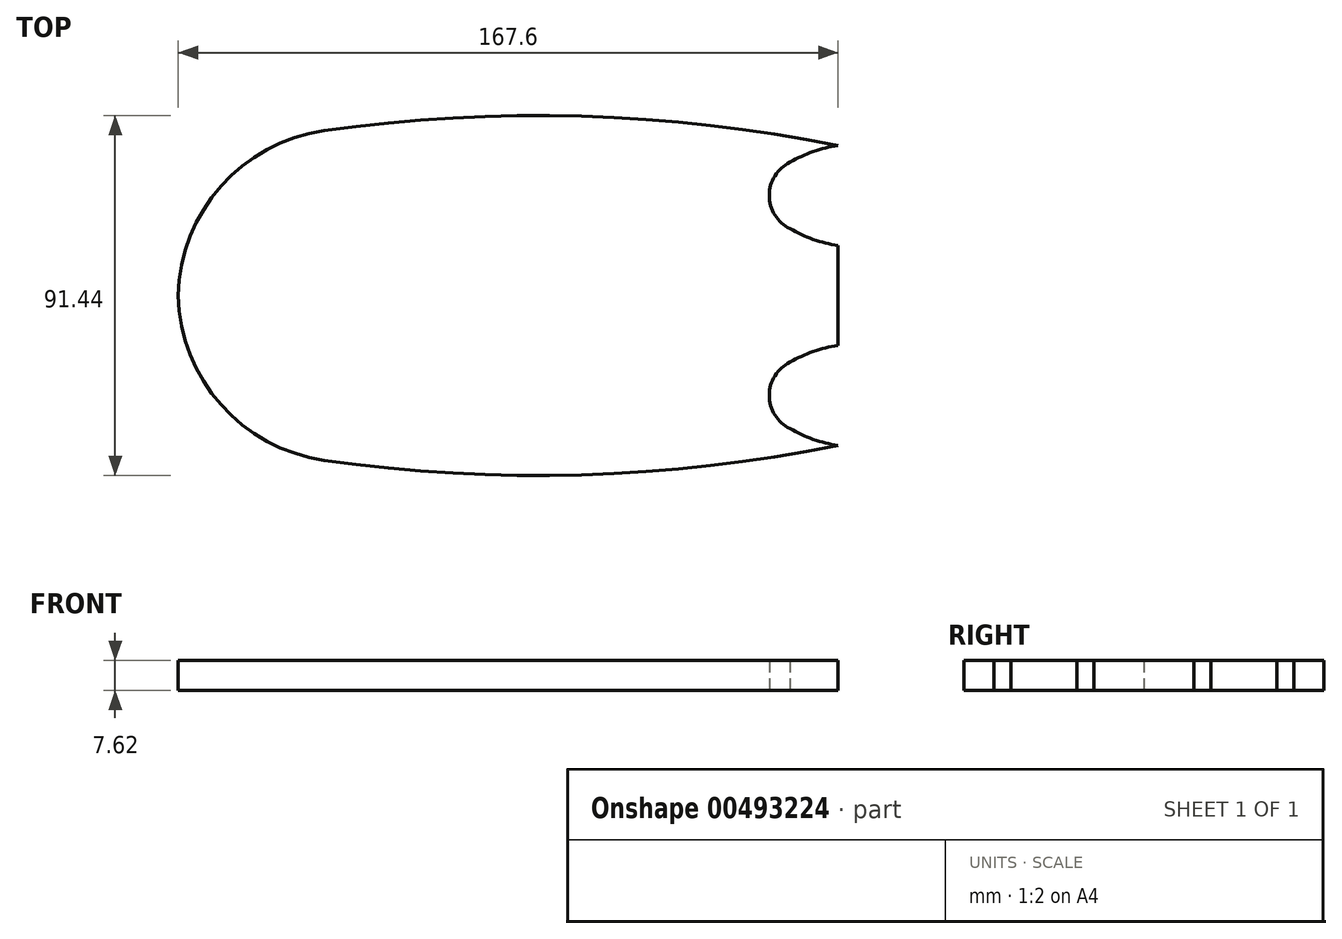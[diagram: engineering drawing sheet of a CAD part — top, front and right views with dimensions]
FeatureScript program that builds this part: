
annotation { "Feature Type Name" : "Feature", "Feature Type Description" : "" }
export const myFeature = defineFeature(function(context is Context, id is Id, definition is map)
    precondition{}
    {
        {
            var Q0;
            Q0=qCreatedBy(makeId("Top.planeOp"),FACE);
            var sketch = newSketch(context, id + "F0", { "sketchPlane" : qUnion([Q0])});
            skLineSegment(sketch, "E0", {"start": v(-87.66, 47.79) * mm, "end": v(-87.66, -28.41) * mm});
            skLineSegment(sketch, "E1", {"start": v(-87.66, -28.41) * mm, "end": v(64.74, -28.41) * mm});
            skLineSegment(sketch, "E2", {"start": v(64.74, -28.41) * mm, "end": v(42.74, -15.71) * mm});
            skLineSegment(sketch, "E3", {"start": v(42.74, -15.71) * mm, "end": v(64.74, -3.01) * mm});
            skLineSegment(sketch, "E4", {"start": v(-87.66, 47.79) * mm, "end": v(64.74, 47.79) * mm});
            skLineSegment(sketch, "E5", {"start": v(64.74, 47.79) * mm, "end": v(42.74, 35.09) * mm});
            skLineSegment(sketch, "E6", {"start": v(42.74, 35.09) * mm, "end": v(64.74, 22.39) * mm});
            skLineSegment(sketch, "E7", {"start": v(64.74, 22.39) * mm, "end": v(64.74, -3.01) * mm});
            skArc(sketch, "E8", {"start": v(64.74, 47.79) * mm, "mid": v(-11.46, 55.4) * mm, "end": v(-87.66, 47.79) * mm});
            skArc(sketch, "E9", {"start": v(-87.66, 47.79) * mm, "mid": v(-102.9, 9.69) * mm, "end": v(-87.66, -28.41) * mm});
            skArc(sketch, "E10", {"start": v(-87.66, -28.41) * mm, "mid": v(-11.46, -36.03) * mm, "end": v(64.74, -28.41) * mm});
            skArc(sketch, "E11", {"start": v(42.74, -15.71) * mm, "mid": v(52.54, -24.15) * mm, "end": v(64.74, -28.41) * mm});
            skArc(sketch, "E12", {"start": v(64.74, -3.01) * mm, "mid": v(52.54, -7.27) * mm, "end": v(42.74, -15.71) * mm});
            skArc(sketch, "E13", {"start": v(52.54, -7.27) * mm, "mid": v(47.27, -15.71) * mm, "end": v(52.54, -24.15) * mm});
            skArc(sketch, "E14", {"start": v(42.74, 35.09) * mm, "mid": v(52.54, 26.65) * mm, "end": v(64.74, 22.39) * mm});
            skArc(sketch, "E15", {"start": v(64.74, 47.79) * mm, "mid": v(52.54, 43.53) * mm, "end": v(42.74, 35.09) * mm});
            skArc(sketch, "E16", {"start": v(52.54, 43.53) * mm, "mid": v(47.27, 35.09) * mm, "end": v(52.54, 26.65) * mm});
            skSolve(sketch);
        }
        {
            var Q0;
            Q0=makeQuery(id+"F0.imprint","IMPRINT",FACE,{"disambiguationData":[TD([[makeQuery(id+"F0.imprint","IMPRINT",EDGE,{"derivedFrom":sQuery(id+"F0.wireOp",EDGE,"E4")}),1.0]])]});
            var Q1;
            Q1=makeQuery(id+"F0.imprint","IMPRINT",FACE,{"disambiguationData":[TD([[makeQuery(id+"F0.imprint","IMPRINT",EDGE,{"derivedFrom":sQuery(id+"F0.wireOp",EDGE,"E0")}),-1.0]])]});
            var Q2;
            Q2=makeQuery(id+"F0.imprint","IMPRINT",FACE,{"disambiguationData":[TD([[makeQuery(id+"F0.imprint","IMPRINT",EDGE,{"derivedFrom":sQuery(id+"F0.wireOp",EDGE,"E0")}),1.0]])]});
            var Q3;
            Q3=makeQuery(id+"F0.imprint","IMPRINT",FACE,{"disambiguationData":[TD([[makeQuery(id+"F0.imprint","IMPRINT",EDGE,{"derivedFrom":sQuery(id+"F0.wireOp",EDGE,"E1")}),-1.0]])]});
            var Q4;
            {var subQ1=sQuery(id+"F0.wireOp",EDGE,"E2");var subQ3=sQuery(id+"F0.wireOp",EDGE,"E13");var subQ4=makeQuery(id+"F0.imprint","INTERSECT",VERTEX,{"derivedFrom":[subQ1,subQ3]});Q4=makeQuery(id+"F0.imprint","IMPRINT",FACE,{"disambiguationData":[TD([[makeQuery(id+"F0.imprint","IMPRINT",EDGE,{"disambiguationData":[TD([[subQ4,-1.0]])],"derivedFrom":subQ3}),-1.0]])]});}
            var Q5;
            {var subQ1=sQuery(id+"F0.wireOp",EDGE,"E2");var subQ3=sQuery(id+"F0.wireOp",EDGE,"E13");var subQ4=makeQuery(id+"F0.imprint","INTERSECT",VERTEX,{"derivedFrom":[subQ1,subQ3]});Q5=makeQuery(id+"F0.imprint","IMPRINT",FACE,{"disambiguationData":[TD([[makeQuery(id+"F0.imprint","IMPRINT",EDGE,{"disambiguationData":[TD([[subQ4,1.0]])],"derivedFrom":subQ3}),-1.0]])]});}
            var Q6;
            {var subQ1=sQuery(id+"F0.wireOp",EDGE,"E3");var subQ3=sQuery(id+"F0.wireOp",EDGE,"E13");var subQ4=makeQuery(id+"F0.imprint","INTERSECT",VERTEX,{"derivedFrom":[subQ1,subQ3]});Q6=makeQuery(id+"F0.imprint","IMPRINT",FACE,{"disambiguationData":[TD([[makeQuery(id+"F0.imprint","IMPRINT",EDGE,{"disambiguationData":[TD([[subQ4,1.0]])],"derivedFrom":subQ3}),-1.0]])]});}
            var Q7;
            {var subQ1=sQuery(id+"F0.wireOp",EDGE,"E5");var subQ3=sQuery(id+"F0.wireOp",EDGE,"E16");var subQ4=makeQuery(id+"F0.imprint","INTERSECT",VERTEX,{"derivedFrom":[subQ1,subQ3]});Q7=makeQuery(id+"F0.imprint","IMPRINT",FACE,{"disambiguationData":[TD([[makeQuery(id+"F0.imprint","IMPRINT",EDGE,{"disambiguationData":[TD([[subQ4,1.0]])],"derivedFrom":subQ3}),-1.0]])]});}
            var Q8;
            {var subQ1=sQuery(id+"F0.wireOp",EDGE,"E5");var subQ3=sQuery(id+"F0.wireOp",EDGE,"E16");var subQ4=makeQuery(id+"F0.imprint","INTERSECT",VERTEX,{"derivedFrom":[subQ1,subQ3]});Q8=makeQuery(id+"F0.imprint","IMPRINT",FACE,{"disambiguationData":[TD([[makeQuery(id+"F0.imprint","IMPRINT",EDGE,{"disambiguationData":[TD([[subQ4,-1.0]])],"derivedFrom":subQ3}),-1.0]])]});}
            var Q9;
            {var subQ1=sQuery(id+"F0.wireOp",EDGE,"E6");var subQ3=sQuery(id+"F0.wireOp",EDGE,"E16");var subQ4=makeQuery(id+"F0.imprint","INTERSECT",VERTEX,{"derivedFrom":[subQ1,subQ3]});Q9=makeQuery(id+"F0.imprint","IMPRINT",FACE,{"disambiguationData":[TD([[makeQuery(id+"F0.imprint","IMPRINT",EDGE,{"disambiguationData":[TD([[subQ4,-1.0]])],"derivedFrom":subQ3}),-1.0]])]});}
            extrude(context, id + "F1", {"entities" : qUnion([Q0, Q1, Q2, Q3, Q4, Q5, Q6, Q7, Q8, Q9]), "depth" : 7.62 * mm});
        }
        {
            var Q0;
            Q0=makeQuery(id+"F1.opExtrude","SWEPT_EDGE",EDGE,{"disambiguationData":[OSD([sQuery(id+"F0.wireOp",EDGE,"E0"),sQuery(id+"F0.wireOp",EDGE,"E1"),sQuery(id+"F0.wireOp",EDGE,"E9"),sQuery(id+"F0.wireOp",EDGE,"E10")])]});
            var Q1;
            Q1=makeQuery(id+"F1.opExtrude","SWEPT_EDGE",EDGE,{"disambiguationData":[OSD([sQuery(id+"F0.wireOp",EDGE,"E0"),sQuery(id+"F0.wireOp",EDGE,"E4"),sQuery(id+"F0.wireOp",EDGE,"E8"),sQuery(id+"F0.wireOp",EDGE,"E9")])]});
            fillet(context, id + "F2", {"entities" : qUnion([Q0, Q1]), "radius" : 43.18 * mm, "tangentPropagation" : true, "allowEdgeOverflow" : false});
        }
    });
